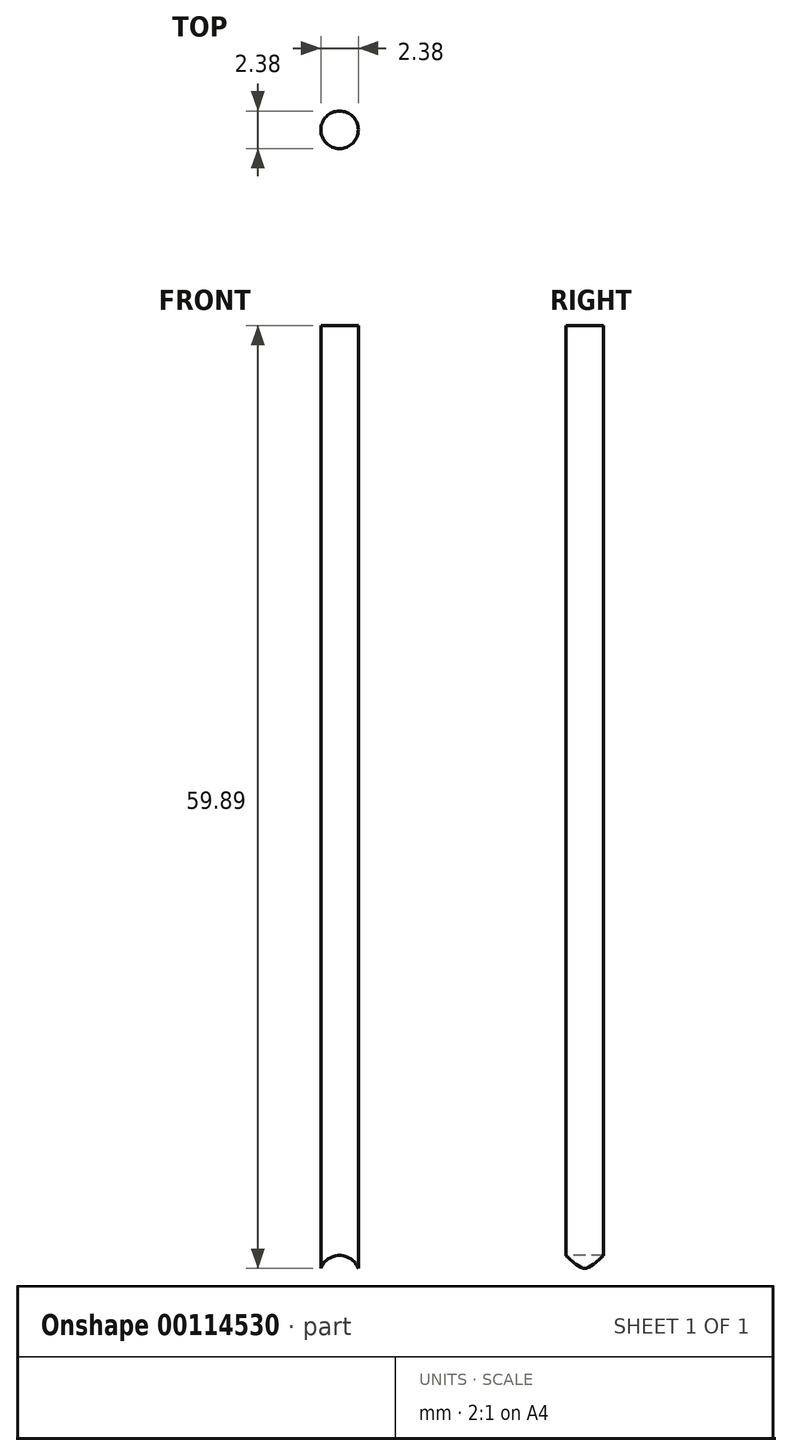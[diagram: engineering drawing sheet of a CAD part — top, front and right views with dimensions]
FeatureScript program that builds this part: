
annotation { "Feature Type Name" : "Feature", "Feature Type Description" : "" }
export const myFeature = defineFeature(function(context is Context, id is Id, definition is map)
    precondition{}
    {
        {
            var Q0;
            Q0=qCreatedBy(makeId("Top.planeOp"),FACE);
            var sketch = newSketch(context, id + "F0", { "sketchPlane" : qUnion([Q0])});
            skCircle(sketch, "E0", {"center": v(0, 0) * mm, "radius": 1.2 * mm});
            skSolve(sketch);
        }
        {
            var Q0;
            Q0=qSketchRegion(id+"F0",true);
            extrude(context, id + "F1", {"entities" : qUnion([Q0]), "depth" : 60.32 * mm});
        }
        {
            var Q0;
            Q0=qCreatedBy(makeId("Front.planeOp"),FACE);
            var sketch = newSketch(context, id + "F2", { "sketchPlane" : qUnion([Q0])});
            skCircle(sketch, "E1", {"center": v(0, 0) * mm, "radius": 1.27 * mm});
            skSolve(sketch);
        }
        {
            var Q0;
            Q0=qSketchRegion(id+"F2",true);
            extrude(context, id + "F3", {"entities" : qUnion([Q0]), "operationType" : NewBodyOperationType.REMOVE, "endBound" : BoundingType.SYMMETRIC, "oppositeDirection" : true, "depth" : 25.4 * mm});
        }
    });
